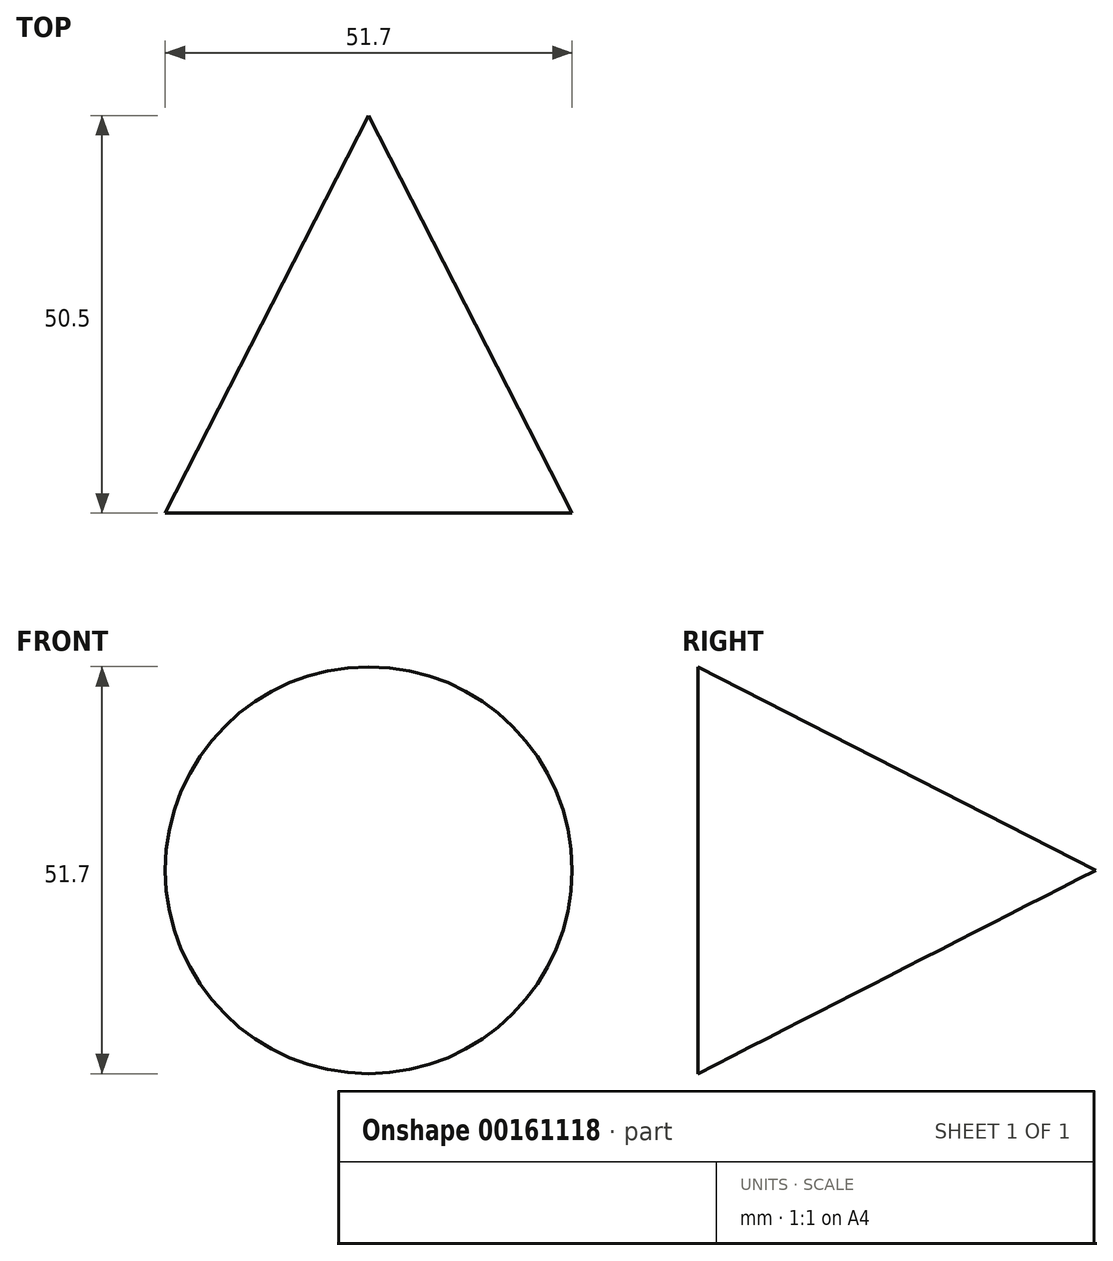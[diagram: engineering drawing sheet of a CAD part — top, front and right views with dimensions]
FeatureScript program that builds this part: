
annotation { "Feature Type Name" : "Feature", "Feature Type Description" : "" }
export const myFeature = defineFeature(function(context is Context, id is Id, definition is map)
    precondition{}
    {
        {
            var Q0;
            Q0=qCreatedBy(makeId("Top.planeOp"),FACE);
            var sketch = newSketch(context, id + "F0", { "sketchPlane" : qUnion([Q0])});
            skLineSegment(sketch, "E0", {"start": v(0, 50.5) * mm, "end": v(25.85, 0) * mm});
            skLineSegment(sketch, "E1", {"start": v(0, 50.5) * mm, "end": v(0, 0) * mm, "construction": true});
            skLineSegment(sketch, "E2", {"start": v(0, 0) * mm, "end": v(25.85, 0) * mm});
            skSolve(sketch);
        }
        {
            var Q0;
            Q0=sQuery(id+"F0.wireOp",EDGE,"E0");
            var Q1;
            Q1=sQuery(id+"F0.wireOp",EDGE,"E2");
            var Q2;
            Q2=sQuery(id+"F0.wireOp",EDGE,"E1");
            revolve(context, id + "F1", {"bodyType" : ToolBodyType.SURFACE, "surfaceEntities" : qUnion([Q0, Q1]), "axis" : qUnion([Q2]), "revolveType" : RevolveType.FULL});
        }
    });
